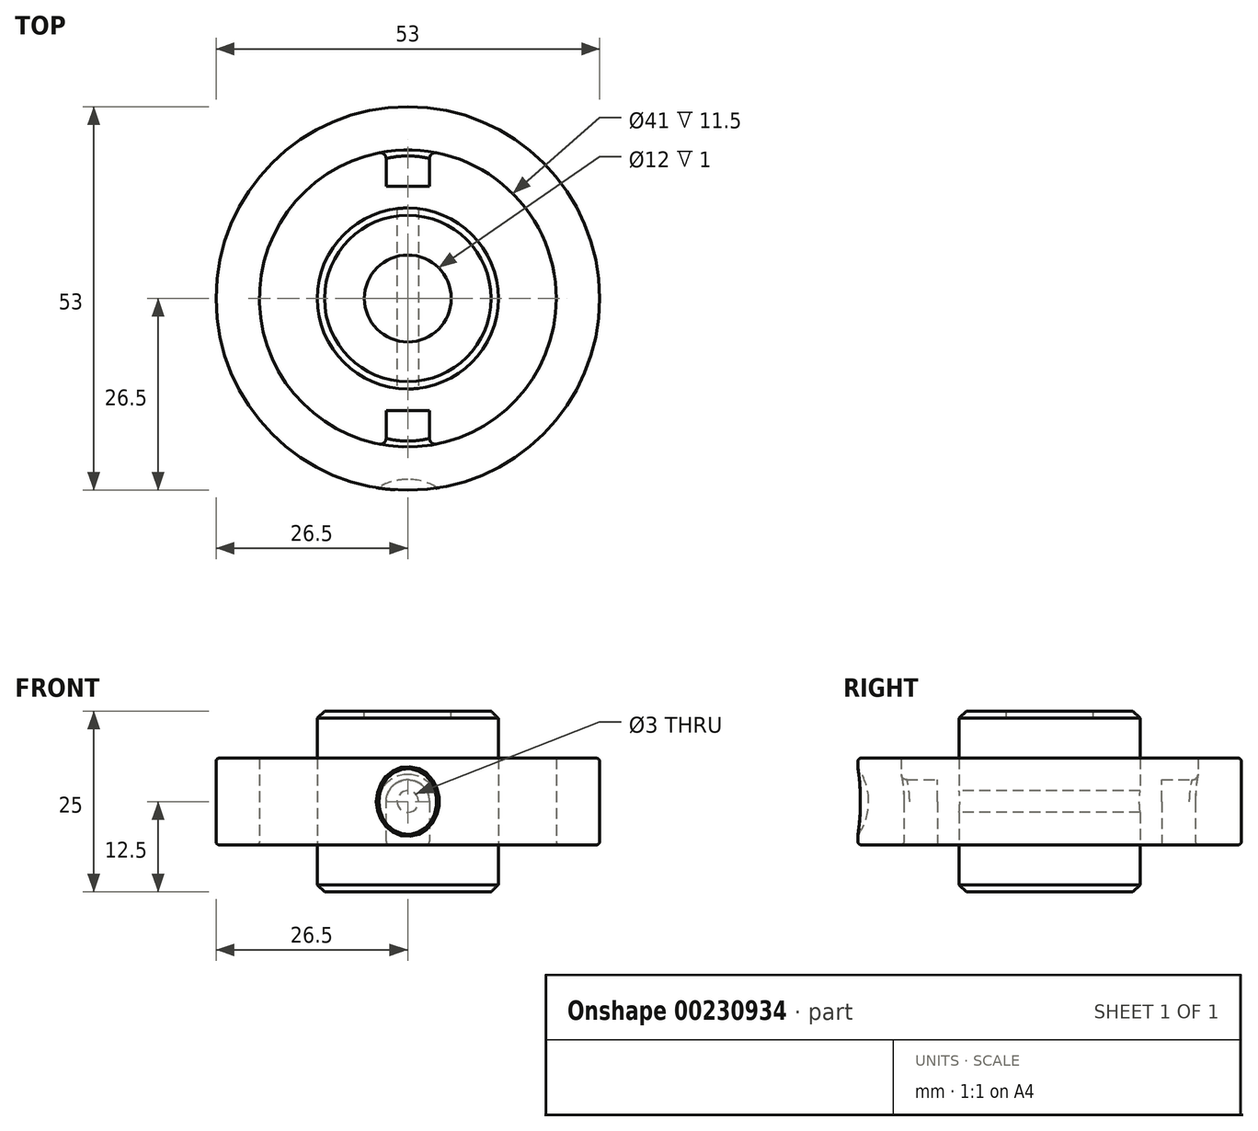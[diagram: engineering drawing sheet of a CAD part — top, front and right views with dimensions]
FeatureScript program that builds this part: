
annotation { "Feature Type Name" : "Feature", "Feature Type Description" : "" }
export const myFeature = defineFeature(function(context is Context, id is Id, definition is map)
    precondition{}
    {
        {
            var Q0;
            Q0=qCreatedBy(makeId("Top.planeOp"),FACE);
            var sketch = newSketch(context, id + "F0", { "sketchPlane" : qUnion([Q0])});
            skCircle(sketch, "E0", {"center": v(0, 0) * mm, "radius": 12.5 * mm});
            skSolve(sketch);
        }
        {
            var Q0;
            Q0=qSketchRegion(id+"F0",true);
            extrude(context, id + "F1", {"entities" : qUnion([Q0]), "depth" : 25 * mm});
        }
        {
            var Q0;
            Q0=makeQuery(id+"F1.opExtrude","CAP_FACE",FACE,{"disambiguationData":[OSD([sQuery(id+"F0.wireOp",EDGE,"E0")])],"isStart":false});
            var sketch = newSketch(context, id + "F2", { "sketchPlane" : qUnion([Q0])});
            skCircle(sketch, "E1", {"center": v(0, 0) * mm, "radius": 6 * mm});
            skSolve(sketch);
        }
        {
            var Q0;
            Q0=qSketchRegion(id+"F2",true);
            extrude(context, id + "F3", {"entities" : qUnion([Q0]), "operationType" : NewBodyOperationType.REMOVE, "oppositeDirection" : true, "depth" : 1 * mm});
        }
        {
            var Q0;
            Q0=qCreatedBy(makeId("Front.planeOp"),FACE);
            var sketch = newSketch(context, id + "F4", { "sketchPlane" : qUnion([Q0])});
            skLineSegment(sketch, "E2", {"start": v(0, 0) * mm, "end": v(0, 12.5) * mm});
            skCircle(sketch, "E3", {"center": v(0, 12.5) * mm, "radius": 1.5 * mm});
            skSolve(sketch);
        }
        {
            var Q0;
            Q0=qSketchRegion(id+"F4",true);
            extrude(context, id + "F5", {"entities" : qUnion([Q0]), "operationType" : NewBodyOperationType.REMOVE, "oppositeDirection" : true, "depth" : 25 * mm, "hasSecondDirection" : true, "secondDirectionOppositeDirection" : false, "secondDirectionDepth" : 25 * mm});
        }
        {
            var Q0;
            Q0=makeQuery(id+"F1.opExtrude","CAP_EDGE",EDGE,{"disambiguationData":[OSD([sQuery(id+"F0.wireOp",EDGE,"E0")])],"isStart":true});
            var Q1;
            Q1=makeQuery(id+"F1.opExtrude","CAP_EDGE",EDGE,{"disambiguationData":[OSD([sQuery(id+"F0.wireOp",EDGE,"E0")])],"isStart":false});
            chamfer(context, id + "F6", {"entities" : qUnion([Q0, Q1]), "width" : 1 * mm, "tangentPropagation" : true});
        }
        {
            var Q0;
            Q0=qCreatedBy(makeId("Top.planeOp"),FACE);
            cPlane(context, id + "F7", {"entities" : qUnion([Q0]), "cplaneType" : CPlaneType.OFFSET, "offset" : 12.5 * mm, "width" : 150 * mm, "height" : 150 * mm});
        }
        {
            var Q0;
            Q0=qCreatedBy(id+"F7.planeOp",FACE);
            var sketch = newSketch(context, id + "F8", { "sketchPlane" : qUnion([Q0])});
            skCircle(sketch, "E4", {"center": v(0, 0) * mm, "radius": 20.5 * mm});
            skCircle(sketch, "E5", {"center": v(0, 0) * mm, "radius": 26.5 * mm});
            skLineSegment(sketch, "E6.bottom", {"start": v(-3, -32.92) * mm, "end": v(3, -32.92) * mm});
            skLineSegment(sketch, "E6.top", {"start": v(-3, 32.92) * mm, "end": v(3, 32.92) * mm});
            skLineSegment(sketch, "E6.left", {"start": v(-3, -32.92) * mm, "end": v(-3, 32.92) * mm});
            skLineSegment(sketch, "E6.right", {"start": v(3, -32.92) * mm, "end": v(3, 32.92) * mm});
            skLineSegment(sketch, "E7.bottom", {"start": v(-4.52, -15.5) * mm, "end": v(4.52, -15.5) * mm});
            skLineSegment(sketch, "E7.top", {"start": v(-4.52, 15.5) * mm, "end": v(4.52, 15.5) * mm});
            skLineSegment(sketch, "E7.left", {"start": v(-4.52, -15.5) * mm, "end": v(-4.52, 15.5) * mm});
            skLineSegment(sketch, "E7.right", {"start": v(4.52, -15.5) * mm, "end": v(4.52, 15.5) * mm});
            skSolve(sketch);
        }
        {
            var Q0;
            {var subQ0=sQuery(id+"F8.wireOp",EDGE,"E6.left");var subQ1=sQuery(id+"F8.wireOp",EDGE,"E4");var subQ2=makeQuery(id+"F8.imprint","INTERSECT",VERTEX,{"disambiguationData":[OD(0.0)],"derivedFrom":[subQ1,subQ0]});Q0=makeQuery(id+"F8.imprint","IMPRINT",FACE,{"disambiguationData":[TD([[makeQuery(id+"F8.imprint","IMPRINT",EDGE,{"disambiguationData":[TD([[subQ2,-1.0]])],"derivedFrom":subQ1}),-1.0]])]});}
            var Q1;
            {var subQ0=sQuery(id+"F8.wireOp",EDGE,"E6.left");var subQ1=sQuery(id+"F8.wireOp",EDGE,"E4");var subQ2=makeQuery(id+"F8.imprint","INTERSECT",VERTEX,{"disambiguationData":[OD(1.0)],"derivedFrom":[subQ1,subQ0]});Q1=makeQuery(id+"F8.imprint","IMPRINT",FACE,{"disambiguationData":[TD([[makeQuery(id+"F8.imprint","IMPRINT",EDGE,{"disambiguationData":[TD([[subQ2,-1.0]])],"derivedFrom":subQ1}),-1.0]])]});}
            var Q2;
            {var subQ0=sQuery(id+"F8.wireOp",EDGE,"E6.left");var subQ1=sQuery(id+"F8.wireOp",EDGE,"E4");var subQ2=makeQuery(id+"F8.imprint","INTERSECT",VERTEX,{"disambiguationData":[OD(1.0)],"derivedFrom":[subQ1,subQ0]});Q2=makeQuery(id+"F8.imprint","IMPRINT",FACE,{"disambiguationData":[TD([[makeQuery(id+"F8.imprint","IMPRINT",EDGE,{"disambiguationData":[TD([[subQ2,-1.0]])],"derivedFrom":subQ1}),1.0]])]});}
            var Q3;
            {var subQ0=sQuery(id+"F8.wireOp",EDGE,"E6.right");var subQ1=sQuery(id+"F8.wireOp",EDGE,"E4");var subQ2=makeQuery(id+"F8.imprint","INTERSECT",VERTEX,{"disambiguationData":[OD(0.0)],"derivedFrom":[subQ1,subQ0]});Q3=makeQuery(id+"F8.imprint","IMPRINT",FACE,{"disambiguationData":[TD([[makeQuery(id+"F8.imprint","IMPRINT",EDGE,{"disambiguationData":[TD([[subQ2,1.0]])],"derivedFrom":subQ1}),-1.0]])]});}
            var Q4;
            {var subQ0=sQuery(id+"F8.wireOp",EDGE,"E6.left");var subQ1=sQuery(id+"F8.wireOp",EDGE,"E4");var subQ2=makeQuery(id+"F8.imprint","INTERSECT",VERTEX,{"disambiguationData":[OD(0.0)],"derivedFrom":[subQ1,subQ0]});Q4=makeQuery(id+"F8.imprint","IMPRINT",FACE,{"disambiguationData":[TD([[makeQuery(id+"F8.imprint","IMPRINT",EDGE,{"disambiguationData":[TD([[subQ2,1.0]])],"derivedFrom":subQ1}),1.0]])]});}
            var Q5;
            {var subQ0=sQuery(id+"F8.wireOp",EDGE,"E6.left");var subQ1=sQuery(id+"F8.wireOp",EDGE,"E4");var subQ2=makeQuery(id+"F8.imprint","INTERSECT",VERTEX,{"disambiguationData":[OD(0.0)],"derivedFrom":[subQ1,subQ0]});Q5=makeQuery(id+"F8.imprint","IMPRINT",FACE,{"disambiguationData":[TD([[makeQuery(id+"F8.imprint","IMPRINT",EDGE,{"disambiguationData":[TD([[subQ2,1.0]])],"derivedFrom":subQ1}),-1.0]])]});}
            extrude(context, id + "F9", {"entities" : qUnion([Q0, Q1, Q2, Q3, Q4, Q5]), "depth" : 6 * mm, "hasSecondDirection" : true, "secondDirectionOppositeDirection" : true, "secondDirectionDepth" : 6 * mm});
        }
        {
            var Q0;
            Q0=makeQuery(id+"F9.opExtrude","CAP_FACE",FACE,{"disambiguationData":[OSD([sQuery(id+"F8.wireOp",EDGE,"E4"),sQuery(id+"F8.wireOp",EDGE,"E5"),sQuery(id+"F8.wireOp",EDGE,"E6.left"),sQuery(id+"F8.wireOp",EDGE,"E6.right"),sQuery(id+"F8.wireOp",EDGE,"E7.bottom"),sQuery(id+"F8.wireOp",EDGE,"E7.top")])],"isStart":false});
            var sketch = newSketch(context, id + "F10", { "sketchPlane" : qUnion([Q0])});
            skCircle(sketch, "E8", {"center": v(0, 0) * mm, "radius": 20.5 * mm});
            skCircle(sketch, "E9", {"center": v(0, 0) * mm, "radius": 13.24 * mm});
            skSolve(sketch);
        }
        {
            var Q0;
            Q0 = qSketchRegion(id + "F10", true);
            extrude(context, id + "F11", {"entities" : qUnion([Q0]), "operationType" : NewBodyOperationType.REMOVE, "oppositeDirection" : true, "depth" : 3 * mm});
        }
        {
            var Q0;
            {var subQ0=sQuery(id+"F8.wireOp",EDGE,"E6.left");Q0=makeQuery(id+"F11.boolean.opBoolean","INTERSECT",EDGE,{"derivedFrom":[makeQuery(id+"F9.opExtrude","SWEPT_FACE",FACE,{"disambiguationData":[OSD([subQ0]),TDD([makeQuery(id+"F8.imprint","IMPRINT",EDGE,{"disambiguationData":[TD([[makeQuery(id+"F8.imprint","INTERSECT",VERTEX,{"disambiguationData":[OD(1.0)],"derivedFrom":[sQuery(id+"F8.wireOp",EDGE,"E4"),subQ0]}),-1.0]])],"derivedFrom":subQ0})])]}),makeQuery(id+"F11.opExtrude","CAP_FACE",FACE,{"disambiguationData":[OSD([sQuery(id+"F10.wireOp",EDGE,"E8"),sQuery(id+"F10.wireOp",EDGE,"E9")])],"isStart":false})]});}
            var Q1;
            {var subQ0=sQuery(id+"F8.wireOp",EDGE,"E6.right");Q1=makeQuery(id+"F11.boolean.opBoolean","INTERSECT",EDGE,{"derivedFrom":[makeQuery(id+"F9.opExtrude","SWEPT_FACE",FACE,{"disambiguationData":[OSD([subQ0]),TDD([makeQuery(id+"F8.imprint","IMPRINT",EDGE,{"disambiguationData":[TD([[makeQuery(id+"F8.imprint","INTERSECT",VERTEX,{"disambiguationData":[OD(1.0)],"derivedFrom":[sQuery(id+"F8.wireOp",EDGE,"E4"),subQ0]}),-1.0]])],"derivedFrom":subQ0})])]}),makeQuery(id+"F11.opExtrude","CAP_FACE",FACE,{"disambiguationData":[OSD([sQuery(id+"F10.wireOp",EDGE,"E8"),sQuery(id+"F10.wireOp",EDGE,"E9")])],"isStart":false})]});}
            var Q2;
            {var subQ0=sQuery(id+"F8.wireOp",EDGE,"E6.left");Q2=makeQuery(id+"FxQpREIJXt1QqdQ_2.1.F11.boolean.opBoolean","INTERSECT",EDGE,{"derivedFrom":[makeQuery(id+"F9.opExtrude","SWEPT_FACE",FACE,{"disambiguationData":[OSD([subQ0]),TDD([makeQuery(id+"F8.imprint","IMPRINT",EDGE,{"disambiguationData":[TD([[makeQuery(id+"F8.imprint","INTERSECT",VERTEX,{"disambiguationData":[OD(1.0)],"derivedFrom":[sQuery(id+"F8.wireOp",EDGE,"E4"),subQ0]}),-1.0]])],"derivedFrom":subQ0})])]}),makeQuery(id+"FxQpREIJXt1QqdQ_2.1.F11.opExtrude","CAP_FACE",FACE,{"disambiguationData":[OSD([sQuery(id+"F10.wireOp",EDGE,"E8"),sQuery(id+"F10.wireOp",EDGE,"E9")])],"isStart":false})]});}
            var Q3;
            {var subQ0=sQuery(id+"F8.wireOp",EDGE,"E6.right");Q3=makeQuery(id+"FxQpREIJXt1QqdQ_2.1.F11.boolean.opBoolean","INTERSECT",EDGE,{"derivedFrom":[makeQuery(id+"F9.opExtrude","SWEPT_FACE",FACE,{"disambiguationData":[OSD([subQ0]),TDD([makeQuery(id+"F8.imprint","IMPRINT",EDGE,{"disambiguationData":[TD([[makeQuery(id+"F8.imprint","INTERSECT",VERTEX,{"disambiguationData":[OD(1.0)],"derivedFrom":[sQuery(id+"F8.wireOp",EDGE,"E4"),subQ0]}),-1.0]])],"derivedFrom":subQ0})])]}),makeQuery(id+"FxQpREIJXt1QqdQ_2.1.F11.opExtrude","CAP_FACE",FACE,{"disambiguationData":[OSD([sQuery(id+"F10.wireOp",EDGE,"E8"),sQuery(id+"F10.wireOp",EDGE,"E9")])],"isStart":false})]});}
            var Q4;
            {var subQ0=sQuery(id+"F8.wireOp",EDGE,"E6.left");Q4=makeQuery(id+"FxQpREIJXt1QqdQ_2.1.F11.boolean.opBoolean","INTERSECT",EDGE,{"derivedFrom":[makeQuery(id+"F9.opExtrude","SWEPT_FACE",FACE,{"disambiguationData":[OSD([subQ0]),TDD([makeQuery(id+"F8.imprint","IMPRINT",EDGE,{"disambiguationData":[TD([[makeQuery(id+"F8.imprint","INTERSECT",VERTEX,{"disambiguationData":[OD(0.0)],"derivedFrom":[sQuery(id+"F8.wireOp",EDGE,"E4"),subQ0]}),1.0]])],"derivedFrom":subQ0})])]}),makeQuery(id+"FxQpREIJXt1QqdQ_2.1.F11.opExtrude","CAP_FACE",FACE,{"disambiguationData":[OSD([sQuery(id+"F10.wireOp",EDGE,"E8"),sQuery(id+"F10.wireOp",EDGE,"E9")])],"isStart":false})]});}
            var Q5;
            {var subQ0=sQuery(id+"F8.wireOp",EDGE,"E6.left");Q5=makeQuery(id+"F11.boolean.opBoolean","INTERSECT",EDGE,{"derivedFrom":[makeQuery(id+"F9.opExtrude","SWEPT_FACE",FACE,{"disambiguationData":[OSD([subQ0]),TDD([makeQuery(id+"F8.imprint","IMPRINT",EDGE,{"disambiguationData":[TD([[makeQuery(id+"F8.imprint","INTERSECT",VERTEX,{"disambiguationData":[OD(0.0)],"derivedFrom":[sQuery(id+"F8.wireOp",EDGE,"E4"),subQ0]}),1.0]])],"derivedFrom":subQ0})])]}),makeQuery(id+"F11.opExtrude","CAP_FACE",FACE,{"disambiguationData":[OSD([sQuery(id+"F10.wireOp",EDGE,"E8"),sQuery(id+"F10.wireOp",EDGE,"E9")])],"isStart":false})]});}
            var Q6;
            {var subQ0=sQuery(id+"F8.wireOp",EDGE,"E6.right");Q6=makeQuery(id+"FxQpREIJXt1QqdQ_2.1.F11.boolean.opBoolean","INTERSECT",EDGE,{"derivedFrom":[makeQuery(id+"F9.opExtrude","SWEPT_FACE",FACE,{"disambiguationData":[OSD([subQ0]),TDD([makeQuery(id+"F8.imprint","IMPRINT",EDGE,{"disambiguationData":[TD([[makeQuery(id+"F8.imprint","INTERSECT",VERTEX,{"disambiguationData":[OD(0.0)],"derivedFrom":[sQuery(id+"F8.wireOp",EDGE,"E4"),subQ0]}),1.0]])],"derivedFrom":subQ0})])]}),makeQuery(id+"FxQpREIJXt1QqdQ_2.1.F11.opExtrude","CAP_FACE",FACE,{"disambiguationData":[OSD([sQuery(id+"F10.wireOp",EDGE,"E8"),sQuery(id+"F10.wireOp",EDGE,"E9")])],"isStart":false})]});}
            var Q7;
            {var subQ0=sQuery(id+"F8.wireOp",EDGE,"E6.right");Q7=makeQuery(id+"F11.boolean.opBoolean","INTERSECT",EDGE,{"derivedFrom":[makeQuery(id+"F9.opExtrude","SWEPT_FACE",FACE,{"disambiguationData":[OSD([subQ0]),TDD([makeQuery(id+"F8.imprint","IMPRINT",EDGE,{"disambiguationData":[TD([[makeQuery(id+"F8.imprint","INTERSECT",VERTEX,{"disambiguationData":[OD(0.0)],"derivedFrom":[sQuery(id+"F8.wireOp",EDGE,"E4"),subQ0]}),1.0]])],"derivedFrom":subQ0})])]}),makeQuery(id+"F11.opExtrude","CAP_FACE",FACE,{"disambiguationData":[OSD([sQuery(id+"F10.wireOp",EDGE,"E8"),sQuery(id+"F10.wireOp",EDGE,"E9")])],"isStart":false})]});}
            fillet(context, id + "F12", {"entities" : qUnion([Q0, Q1, Q2, Q3, Q4, Q5, Q6, Q7]), "radius" : 3 * mm, "tangentPropagation" : true, "allowEdgeOverflow" : false});
        }
        {
            var Q0;
            Q0=qCreatedBy(id+"F7.planeOp",FACE);
            var sketch = newSketch(context, id + "F13", { "sketchPlane" : qUnion([Q0])});
            skCircle(sketch, "E10", {"center": v(0, -33) * mm, "radius": 8 * mm});
            skLineSegment(sketch, "E11", {"start": v(0, -25) * mm, "end": v(0, -41) * mm});
            skSolve(sketch);
        }
        {
            var Q0;
            {var subQ0=sQuery(id+"F13.wireOp",EDGE,"E11");Q0=makeQuery(id+"F13.imprint","IMPRINT",FACE,{"disambiguationData":[TD([[makeQuery(id+"F13.imprint","IMPRINT",EDGE,{"derivedFrom":subQ0}),1.0]])]});}
            var Q1;
            Q1=sQuery(id+"F13.wireOp",EDGE,"E11");
            revolve(context, id + "F14", {"operationType" : NewBodyOperationType.REMOVE, "entities" : qUnion([Q0]), "axis" : qUnion([Q1]), "revolveType" : RevolveType.FULL, "oppositeDirection" : true});
        }
        {
            var Q0;
            {var subQ0=sQuery(id+"F10.wireOp",EDGE,"E8");var subQ1=sQuery(id+"F8.wireOp",EDGE,"E6.right");var subQ2=sQuery(id+"F8.wireOp",EDGE,"E4");var subQ3=sQuery(id+"F8.wireOp",EDGE,"E6.left");var subQ4=makeQuery(id+"F8.imprint","INTERSECT",VERTEX,{"disambiguationData":[OD(0.0)],"derivedFrom":[subQ2,subQ3]});Q0=makeQuery(id+"F12.opFillet","BLEND_EDGE",EDGE,{"blendedFrom":[makeQuery(id+"F11.boolean.opBoolean","INTERSECT",EDGE,{"derivedFrom":[makeQuery(id+"F9.opExtrude","SWEPT_FACE",FACE,{"disambiguationData":[OSD([subQ3]),TDD([makeQuery(id+"F8.imprint","IMPRINT",EDGE,{"disambiguationData":[TD([[subQ4,1.0]])],"derivedFrom":subQ3})])]}),makeQuery(id+"F11.opExtrude","CAP_FACE",FACE,{"disambiguationData":[OSD([subQ0,sQuery(id+"F10.wireOp",EDGE,"E9")])],"isStart":false})]}),makeQuery(id+"FxQpREIJXt1QqdQ_2.1.F11.boolean.opBoolean","MERGE",FACE,{"derivedFrom":[makeQuery(id+"F11.boolean.opBoolean","MERGE",FACE,{"derivedFrom":[makeQuery(id+"F9.opExtrude","SWEPT_FACE",FACE,{"disambiguationData":[OSD([subQ2]),TDD([makeQuery(id+"F8.imprint","IMPRINT",EDGE,{"disambiguationData":[TD([[subQ4,-1.0]])],"derivedFrom":subQ2})])]}),makeQuery(id+"F9.opExtrude","SWEPT_FACE",FACE,{"disambiguationData":[OSD([subQ2]),TDD([makeQuery(id+"F8.imprint","IMPRINT",EDGE,{"disambiguationData":[TD([[makeQuery(id+"F8.imprint","INTERSECT",VERTEX,{"disambiguationData":[OD(0.0)],"derivedFrom":[subQ2,subQ1]}),1.0]])],"derivedFrom":subQ2})])]}),makeQuery(id+"F11.opExtrude","SWEPT_FACE",FACE,{"disambiguationData":[OSD([subQ0])]})]}),makeQuery(id+"FxQpREIJXt1QqdQ_2.1.F11.opExtrude","SWEPT_FACE",FACE,{"disambiguationData":[OSD([subQ0])]})]})],"blendedInto":[makeQuery(id+"FxQpREIJXt1QqdQ_2.1.F11.boolean.opBoolean","MERGE",FACE,{"derivedFrom":[makeQuery(id+"F11.boolean.opBoolean","MERGE",FACE,{"derivedFrom":[makeQuery(id+"F9.opExtrude","SWEPT_FACE",FACE,{"disambiguationData":[OSD([subQ2]),TDD([makeQuery(id+"F8.imprint","IMPRINT",EDGE,{"disambiguationData":[TD([[subQ4,-1.0]])],"derivedFrom":subQ2})])]}),makeQuery(id+"F9.opExtrude","SWEPT_FACE",FACE,{"disambiguationData":[OSD([subQ2]),TDD([makeQuery(id+"F8.imprint","IMPRINT",EDGE,{"disambiguationData":[TD([[makeQuery(id+"F8.imprint","INTERSECT",VERTEX,{"disambiguationData":[OD(0.0)],"derivedFrom":[subQ2,subQ1]}),1.0]])],"derivedFrom":subQ2})])]}),makeQuery(id+"F11.opExtrude","SWEPT_FACE",FACE,{"disambiguationData":[OSD([subQ0])]})]}),makeQuery(id+"FxQpREIJXt1QqdQ_2.1.F11.opExtrude","SWEPT_FACE",FACE,{"disambiguationData":[OSD([subQ0])]})]})]});}
            var Q1;
            {var subQ0=sQuery(id+"F10.wireOp",EDGE,"E8");var subQ1=sQuery(id+"F8.wireOp",EDGE,"E6.right");var subQ2=sQuery(id+"F8.wireOp",EDGE,"E4");var subQ3=sQuery(id+"F8.wireOp",EDGE,"E6.left");var subQ4=makeQuery(id+"F8.imprint","INTERSECT",VERTEX,{"disambiguationData":[OD(1.0)],"derivedFrom":[subQ2,subQ3]});Q1=makeQuery(id+"F12.opFillet","BLEND_EDGE",EDGE,{"blendedFrom":[makeQuery(id+"F11.boolean.opBoolean","INTERSECT",EDGE,{"derivedFrom":[makeQuery(id+"F9.opExtrude","SWEPT_FACE",FACE,{"disambiguationData":[OSD([subQ3]),TDD([makeQuery(id+"F8.imprint","IMPRINT",EDGE,{"disambiguationData":[TD([[subQ4,-1.0]])],"derivedFrom":subQ3})])]}),makeQuery(id+"F11.opExtrude","CAP_FACE",FACE,{"disambiguationData":[OSD([subQ0,sQuery(id+"F10.wireOp",EDGE,"E9")])],"isStart":false})]}),makeQuery(id+"FxQpREIJXt1QqdQ_2.1.F11.boolean.opBoolean","MERGE",FACE,{"derivedFrom":[makeQuery(id+"F11.boolean.opBoolean","MERGE",FACE,{"derivedFrom":[makeQuery(id+"F9.opExtrude","SWEPT_FACE",FACE,{"disambiguationData":[OSD([subQ2]),TDD([makeQuery(id+"F8.imprint","IMPRINT",EDGE,{"disambiguationData":[TD([[makeQuery(id+"F8.imprint","INTERSECT",VERTEX,{"disambiguationData":[OD(0.0)],"derivedFrom":[subQ2,subQ3]}),-1.0]])],"derivedFrom":subQ2})])]}),makeQuery(id+"F9.opExtrude","SWEPT_FACE",FACE,{"disambiguationData":[OSD([subQ2]),TDD([makeQuery(id+"F8.imprint","IMPRINT",EDGE,{"disambiguationData":[TD([[makeQuery(id+"F8.imprint","INTERSECT",VERTEX,{"disambiguationData":[OD(0.0)],"derivedFrom":[subQ2,subQ1]}),1.0]])],"derivedFrom":subQ2})])]}),makeQuery(id+"F11.opExtrude","SWEPT_FACE",FACE,{"disambiguationData":[OSD([subQ0])]})]}),makeQuery(id+"FxQpREIJXt1QqdQ_2.1.F11.opExtrude","SWEPT_FACE",FACE,{"disambiguationData":[OSD([subQ0])]})]})],"blendedInto":[makeQuery(id+"FxQpREIJXt1QqdQ_2.1.F11.boolean.opBoolean","MERGE",FACE,{"derivedFrom":[makeQuery(id+"F11.boolean.opBoolean","MERGE",FACE,{"derivedFrom":[makeQuery(id+"F9.opExtrude","SWEPT_FACE",FACE,{"disambiguationData":[OSD([subQ2]),TDD([makeQuery(id+"F8.imprint","IMPRINT",EDGE,{"disambiguationData":[TD([[makeQuery(id+"F8.imprint","INTERSECT",VERTEX,{"disambiguationData":[OD(0.0)],"derivedFrom":[subQ2,subQ3]}),-1.0]])],"derivedFrom":subQ2})])]}),makeQuery(id+"F9.opExtrude","SWEPT_FACE",FACE,{"disambiguationData":[OSD([subQ2]),TDD([makeQuery(id+"F8.imprint","IMPRINT",EDGE,{"disambiguationData":[TD([[makeQuery(id+"F8.imprint","INTERSECT",VERTEX,{"disambiguationData":[OD(0.0)],"derivedFrom":[subQ2,subQ1]}),1.0]])],"derivedFrom":subQ2})])]}),makeQuery(id+"F11.opExtrude","SWEPT_FACE",FACE,{"disambiguationData":[OSD([subQ0])]})]}),makeQuery(id+"FxQpREIJXt1QqdQ_2.1.F11.opExtrude","SWEPT_FACE",FACE,{"disambiguationData":[OSD([subQ0])]})]})]});}
            fillet(context, id + "F15", {"entities" : qUnion([Q0, Q1]), "radius" : 0.8 * mm, "tangentPropagation" : true, "allowEdgeOverflow" : false});
        }
        {
            var Q0;
            {var subQ0=sQuery(id+"F8.wireOp",EDGE,"E6.right");var subQ1=sQuery(id+"F8.wireOp",EDGE,"E4");var subQ2=sQuery(id+"F8.wireOp",EDGE,"E6.left");Q0=makeQuery(id+"F11.boolean.opBoolean","MERGE",EDGE,{"derivedFrom":[makeQuery(id+"F9.opExtrude","CAP_EDGE",EDGE,{"disambiguationData":[OSD([subQ1]),TDD([makeQuery(id+"F8.imprint","IMPRINT",EDGE,{"disambiguationData":[TD([[makeQuery(id+"F8.imprint","INTERSECT",VERTEX,{"disambiguationData":[OD(0.0)],"derivedFrom":[subQ1,subQ2]}),-1.0]])],"derivedFrom":subQ1})])],"isStart":false}),makeQuery(id+"F9.opExtrude","CAP_EDGE",EDGE,{"disambiguationData":[OSD([subQ1]),TDD([makeQuery(id+"F8.imprint","IMPRINT",EDGE,{"disambiguationData":[TD([[makeQuery(id+"F8.imprint","INTERSECT",VERTEX,{"disambiguationData":[OD(0.0)],"derivedFrom":[subQ1,subQ0]}),1.0]])],"derivedFrom":subQ1})])],"isStart":false}),makeQuery(id+"F11.opExtrude","CAP_EDGE",EDGE,{"disambiguationData":[OSD([sQuery(id+"F10.wireOp",EDGE,"E8")])],"isStart":true})]});}
            var Q1;
            Q1=makeQuery(id+"F9.opExtrude","CAP_EDGE",EDGE,{"disambiguationData":[OSD([sQuery(id+"F8.wireOp",EDGE,"E5")])],"isStart":false});
            var Q2;
            Q2=makeQuery(id+"F9.opExtrude","CAP_EDGE",EDGE,{"disambiguationData":[OSD([sQuery(id+"F8.wireOp",EDGE,"E5")])],"isStart":true});
            var Q3;
            {var subQ0=sQuery(id+"F8.wireOp",EDGE,"E6.right");var subQ1=sQuery(id+"F8.wireOp",EDGE,"E4");var subQ2=sQuery(id+"F8.wireOp",EDGE,"E6.left");Q3=makeQuery(id+"FxQpREIJXt1QqdQ_2.1.F11.boolean.opBoolean","MERGE",EDGE,{"derivedFrom":[makeQuery(id+"F9.opExtrude","CAP_EDGE",EDGE,{"disambiguationData":[OSD([subQ1]),TDD([makeQuery(id+"F8.imprint","IMPRINT",EDGE,{"disambiguationData":[TD([[makeQuery(id+"F8.imprint","INTERSECT",VERTEX,{"disambiguationData":[OD(0.0)],"derivedFrom":[subQ1,subQ2]}),-1.0]])],"derivedFrom":subQ1})])],"isStart":true}),makeQuery(id+"F9.opExtrude","CAP_EDGE",EDGE,{"disambiguationData":[OSD([subQ1]),TDD([makeQuery(id+"F8.imprint","IMPRINT",EDGE,{"disambiguationData":[TD([[makeQuery(id+"F8.imprint","INTERSECT",VERTEX,{"disambiguationData":[OD(0.0)],"derivedFrom":[subQ1,subQ0]}),1.0]])],"derivedFrom":subQ1})])],"isStart":true}),makeQuery(id+"FxQpREIJXt1QqdQ_2.1.F11.opExtrude","CAP_EDGE",EDGE,{"disambiguationData":[OSD([sQuery(id+"F10.wireOp",EDGE,"E8")])],"isStart":true})]});}
            var Q4;
            Q4=makeQuery(id+"F14.boolean.opBoolean","INTERSECT",EDGE,{"derivedFrom":[makeQuery(id+"F9.opExtrude","SWEPT_FACE",FACE,{"disambiguationData":[OSD([sQuery(id+"F8.wireOp",EDGE,"E5")])]}),makeQuery(id+"F14.opRevolve","SWEPT_FACE",FACE,{"disambiguationData":[OSD([sQuery(id+"F13.wireOp",EDGE,"E10")])]})]});
            var Q5;
            Q5=makeQuery(id+"FkjGBC1RzMTZgd8_2.1.F14.boolean.opBoolean","INTERSECT",EDGE,{"derivedFrom":[makeQuery(id+"F9.opExtrude","SWEPT_FACE",FACE,{"disambiguationData":[OSD([sQuery(id+"F8.wireOp",EDGE,"E5")])]}),makeQuery(id+"FkjGBC1RzMTZgd8_2.1.F14.opRevolve","SWEPT_FACE",FACE,{"disambiguationData":[OSD([sQuery(id+"F13.wireOp",EDGE,"E10")])]})]});
            var Q6;
            Q6=makeQuery(id+"FkjGBC1RzMTZgd8_2.2.F14.boolean.opBoolean","INTERSECT",EDGE,{"derivedFrom":[makeQuery(id+"F9.opExtrude","SWEPT_FACE",FACE,{"disambiguationData":[OSD([sQuery(id+"F8.wireOp",EDGE,"E5")])]}),makeQuery(id+"FkjGBC1RzMTZgd8_2.2.F14.opRevolve","SWEPT_FACE",FACE,{"disambiguationData":[OSD([sQuery(id+"F13.wireOp",EDGE,"E10")])]})]});
            fillet(context, id + "F16", {"entities" : qUnion([Q0, Q1, Q2, Q3, Q4, Q5, Q6]), "radius" : 0.5 * mm, "tangentPropagation" : true, "allowEdgeOverflow" : false});
        }
    });
